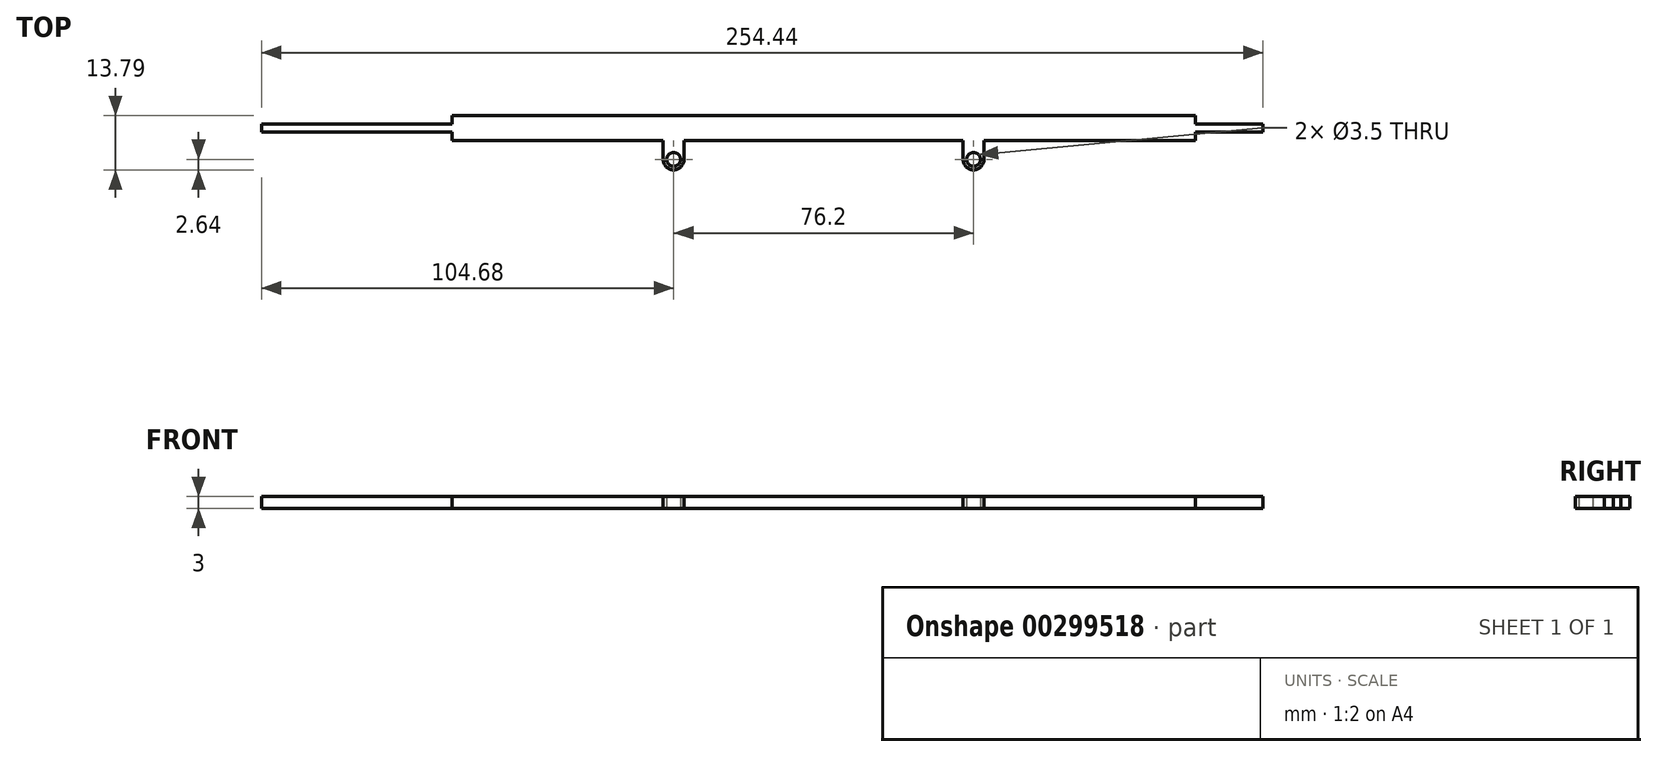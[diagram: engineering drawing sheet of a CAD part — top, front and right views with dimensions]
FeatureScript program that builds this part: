
annotation { "Feature Type Name" : "Feature", "Feature Type Description" : "" }
export const myFeature = defineFeature(function(context is Context, id is Id, definition is map)
    precondition{}
    {
        {
            var Q0;
            Q0=qCreatedBy(makeId("Top.planeOp"),FACE);
            var sketch = newSketch(context, id + "F0", { "sketchPlane" : qUnion([Q0])});
            skLineSegment(sketch, "E0.bottom", {"start": v(129.86, 3.2) * mm, "end": v(-129.86, 3.2) * mm});
            skLineSegment(sketch, "E0.top", {"start": v(129.86, -3.2) * mm, "end": v(-129.86, -3.2) * mm});
            skLineSegment(sketch, "E0.left", {"start": v(129.86, 3.2) * mm, "end": v(129.86, -3.2) * mm});
            skLineSegment(sketch, "E0.right", {"start": v(-129.86, 3.2) * mm, "end": v(-129.86, -3.2) * mm});
            skPoint(sketch, "E0.middle", {"position": v(0, 0) * mm});
            skSolve(sketch);
        }
        {
            var Q0;
            Q0=makeQuery(id+"F0.imprint","IMPRINT",FACE,{"disambiguationData":[TD([[makeQuery(id+"F0.imprint","IMPRINT",EDGE,{"derivedFrom":sQuery(id+"F0.wireOp",EDGE,"E0.bottom")}),1.0]])]});
            extrude(context, id + "F1", {"entities" : qUnion([Q0]), "depth" : 3 * mm});
        }
        {
            var Q0;
            Q0=qCreatedBy(makeId("Top.planeOp"),FACE);
            var sketch = newSketch(context, id + "F2", { "sketchPlane" : qUnion([Q0])});
            skLineSegment(sketch, "E1.bottom", {"start": v(129.86, -3.2) * mm, "end": v(124.58, -3.2) * mm});
            skLineSegment(sketch, "E1.top", {"start": v(129.86, -10.59) * mm, "end": v(124.58, -10.59) * mm});
            skLineSegment(sketch, "E1.left", {"start": v(129.86, -3.2) * mm, "end": v(129.86, -10.59) * mm});
            skLineSegment(sketch, "E1.right", {"start": v(124.58, -3.2) * mm, "end": v(124.58, -10.59) * mm});
            skCircle(sketch, "E2", {"center": v(127.22, -7.95) * mm, "radius": 1.75 * mm});
            skLineSegment(sketch, "E3", {"start": v(127.22, -7.95) * mm, "end": v(127.22, -10.59) * mm});
            skLineSegment(sketch, "E4", {"start": v(127.22, -7.95) * mm, "end": v(124.58, -7.95) * mm});
            skLineSegment(sketch, "E5.bottom", {"start": v(53.66, -3.2) * mm, "end": v(48.38, -3.2) * mm});
            skLineSegment(sketch, "E5.top", {"start": v(53.66, -10.59) * mm, "end": v(48.38, -10.59) * mm});
            skLineSegment(sketch, "E5.left", {"start": v(53.66, -3.2) * mm, "end": v(53.66, -10.59) * mm});
            skLineSegment(sketch, "E5.right", {"start": v(48.38, -3.2) * mm, "end": v(48.38, -10.6) * mm});
            skCircle(sketch, "E6", {"center": v(51.02, -7.95) * mm, "radius": 1.75 * mm});
            skPoint(sketch, "E6.centerSnap0", {"position": v(51.02, -10.6) * mm});
            skLineSegment(sketch, "E7", {"start": v(51.02, -7.95) * mm, "end": v(48.38, -7.95) * mm});
            skPoint(sketch, "E7.endSnap0", {"position": v(48.38, -6.9) * mm});
            skLineSegment(sketch, "E8.bottom", {"start": v(-27.82, -3.2) * mm, "end": v(-22.54, -3.2) * mm});
            skLineSegment(sketch, "E8.top", {"start": v(-27.82, -10.6) * mm, "end": v(-22.54, -10.6) * mm});
            skLineSegment(sketch, "E8.left", {"start": v(-27.82, -3.2) * mm, "end": v(-27.82, -10.6) * mm});
            skLineSegment(sketch, "E8.right", {"start": v(-22.54, -3.2) * mm, "end": v(-22.54, -10.6) * mm});
            skCircle(sketch, "E9", {"center": v(-25.18, -7.95) * mm, "radius": 1.75 * mm});
            skLineSegment(sketch, "E10", {"start": v(-25.18, -7.95) * mm, "end": v(-27.82, -7.95) * mm});
            skSolve(sketch);
        }
        {
            var Q0;
            {var subQ1=sQuery(id+"F2.wireOp",EDGE,"E1.bottom");Q0=makeQuery(id+"F2.imprint","IMPRINT",FACE,{"disambiguationData":[TD([[makeQuery(id+"F2.imprint","IMPRINT",EDGE,{"derivedFrom":subQ1}),1.0]])]});}
            var Q1;
            {var subQ1=sQuery(id+"F2.wireOp",EDGE,"E1.top");var subQ7=sQuery(id+"F2.wireOp",EDGE,"E1.right");var subQ8=makeQuery(id+"F2.imprint","INTERSECT",VERTEX,{"derivedFrom":[subQ1,subQ7]});Q1=makeQuery(id+"F2.imprint","IMPRINT",FACE,{"disambiguationData":[TD([[makeQuery(id+"F2.imprint","IMPRINT",EDGE,{"disambiguationData":[TD([[subQ8,1.0]])],"derivedFrom":subQ1}),-1.0]])]});}
            var Q2;
            {var subQ1=sQuery(id+"F2.wireOp",EDGE,"E5.bottom");Q2=makeQuery(id+"F2.imprint","IMPRINT",FACE,{"disambiguationData":[TD([[makeQuery(id+"F2.imprint","IMPRINT",EDGE,{"derivedFrom":subQ1}),1.0]])]});}
            var Q3;
            {var subQ3=sQuery(id+"F2.wireOp",EDGE,"E8.bottom");Q3=makeQuery(id+"F2.imprint","IMPRINT",FACE,{"disambiguationData":[TD([[makeQuery(id+"F2.imprint","IMPRINT",EDGE,{"derivedFrom":subQ3}),-1.0]])]});}
            extrude(context, id + "F3", {"entities" : qUnion([Q0, Q1, Q2, Q3]), "operationType" : NewBodyOperationType.ADD, "depth" : 3 * mm});
        }
        {
            var Q0;
            Q0=makeQuery(id+"F3.opExtrude","SWEPT_EDGE",EDGE,{"disambiguationData":[OSD([sQuery(id+"F2.wireOp",EDGE,"E5.top"),sQuery(id+"F2.wireOp",EDGE,"E5.right")])]});
            var Q1;
            Q1=makeQuery(id+"F3.opExtrude","SWEPT_EDGE",EDGE,{"disambiguationData":[OSD([sQuery(id+"F2.wireOp",EDGE,"E5.top"),sQuery(id+"F2.wireOp",EDGE,"E5.left")])]});
            var Q2;
            Q2=makeQuery(id+"F3.opExtrude","SWEPT_EDGE",EDGE,{"disambiguationData":[OSD([sQuery(id+"F2.wireOp",EDGE,"E1.top"),sQuery(id+"F2.wireOp",EDGE,"E1.right")])]});
            var Q3;
            Q3=makeQuery(id+"F3.opExtrude","SWEPT_EDGE",EDGE,{"disambiguationData":[OSD([sQuery(id+"F2.wireOp",EDGE,"E1.top"),sQuery(id+"F2.wireOp",EDGE,"E1.left")])]});
            var Q4;
            Q4=makeQuery(id+"F3.opExtrude","SWEPT_EDGE",EDGE,{"disambiguationData":[OSD([sQuery(id+"F2.wireOp",EDGE,"E8.top"),sQuery(id+"F2.wireOp",EDGE,"E8.left")])]});
            var Q5;
            Q5=makeQuery(id+"F3.opExtrude","SWEPT_EDGE",EDGE,{"disambiguationData":[OSD([sQuery(id+"F2.wireOp",EDGE,"E8.top"),sQuery(id+"F2.wireOp",EDGE,"E8.right")])]});
            fillet(context, id + "F4", {"entities" : qUnion([Q0, Q1, Q2, Q3, Q4, Q5]), "radius" : 2.64 * mm, "tangentPropagation" : true, "allowEdgeOverflow" : false});
        }
        {
            var Q0;
            Q0=makeQuery(id+"F3.boolean.opBoolean","MERGE",FACE,{"derivedFrom":[makeQuery(id+"F1.opExtrude","CAP_FACE",FACE,{"disambiguationData":[OSD([sQuery(id+"F0.wireOp",EDGE,"E0.bottom"),sQuery(id+"F0.wireOp",EDGE,"E0.top"),sQuery(id+"F0.wireOp",EDGE,"E0.left"),sQuery(id+"F0.wireOp",EDGE,"E0.right")])],"isStart":false}),makeQuery(id+"F3.opExtrude","CAP_FACE",FACE,{"disambiguationData":[OSD([sQuery(id+"F2.wireOp",EDGE,"E1.bottom"),sQuery(id+"F2.wireOp",EDGE,"E1.top"),sQuery(id+"F2.wireOp",EDGE,"E1.left"),sQuery(id+"F2.wireOp",EDGE,"E1.right"),sQuery(id+"F2.wireOp",EDGE,"E2")])],"isStart":false}),makeQuery(id+"F3.opExtrude","CAP_FACE",FACE,{"disambiguationData":[OSD([sQuery(id+"F2.wireOp",EDGE,"E5.bottom"),sQuery(id+"F2.wireOp",EDGE,"E5.top"),sQuery(id+"F2.wireOp",EDGE,"E5.left"),sQuery(id+"F2.wireOp",EDGE,"E5.right"),sQuery(id+"F2.wireOp",EDGE,"E6")])],"isStart":false}),makeQuery(id+"F3.opExtrude","CAP_FACE",FACE,{"disambiguationData":[OSD([sQuery(id+"F2.wireOp",EDGE,"E8.bottom"),sQuery(id+"F2.wireOp",EDGE,"E8.top"),sQuery(id+"F2.wireOp",EDGE,"E8.left"),sQuery(id+"F2.wireOp",EDGE,"E8.right"),sQuery(id+"F2.wireOp",EDGE,"E9")])],"isStart":false})]});
            var sketch = newSketch(context, id + "F5", { "sketchPlane" : qUnion([Q0])});
            skLineSegment(sketch, "E11.bottom", {"start": v(107.33, 1) * mm, "end": v(124.58, 1) * mm});
            skLineSegment(sketch, "E11.top", {"start": v(107.33, 3.2) * mm, "end": v(124.58, 3.2) * mm});
            skLineSegment(sketch, "E11.left", {"start": v(107.33, 1) * mm, "end": v(107.33, 3.2) * mm});
            skLineSegment(sketch, "E11.right", {"start": v(124.58, 1) * mm, "end": v(124.58, 3.2) * mm});
            skLineSegment(sketch, "E12.bottom", {"start": v(107.33, -3.2) * mm, "end": v(124.58, -3.2) * mm});
            skLineSegment(sketch, "E12.top", {"start": v(107.33, -1) * mm, "end": v(124.58, -1) * mm});
            skLineSegment(sketch, "E12.left", {"start": v(107.33, -3.2) * mm, "end": v(107.33, -1) * mm});
            skLineSegment(sketch, "E12.right", {"start": v(124.58, -3.2) * mm, "end": v(124.58, -1) * mm});
            skLineSegment(sketch, "E13.bottom", {"start": v(124.58, 3.2) * mm, "end": v(129.86, 3.2) * mm});
            skLineSegment(sketch, "E13.top", {"start": v(124.58, -10.59) * mm, "end": v(129.86, -10.59) * mm});
            skLineSegment(sketch, "E13.left", {"start": v(124.58, 3.2) * mm, "end": v(124.58, -10.59) * mm});
            skLineSegment(sketch, "E13.right", {"start": v(129.86, 3.2) * mm, "end": v(129.86, -10.59) * mm});
            skSolve(sketch);
        }
        {
            var Q0;
            {var subQ3=sQuery(id+"F5.wireOp",EDGE,"E13.bottom");Q0=makeQuery(id+"F5.imprint","IMPRINT",FACE,{"disambiguationData":[TD([[makeQuery(id+"F5.imprint","IMPRINT",EDGE,{"derivedFrom":subQ3}),1.0]])]});}
            var Q1;
            {var subQ0=sQuery(id+"F5.wireOp",EDGE,"E11.bottom");Q1=makeQuery(id+"F5.imprint","IMPRINT",FACE,{"disambiguationData":[TD([[makeQuery(id+"F5.imprint","IMPRINT",EDGE,{"derivedFrom":subQ0}),1.0]])]});}
            var Q2;
            {var subQ0=sQuery(id+"F5.wireOp",EDGE,"E12.bottom");Q2=makeQuery(id+"F5.imprint","IMPRINT",FACE,{"disambiguationData":[TD([[makeQuery(id+"F5.imprint","IMPRINT",EDGE,{"derivedFrom":subQ0}),-1.0]])]});}
            extrude(context, id + "F6", {"entities" : qUnion([Q0, Q1, Q2]), "operationType" : NewBodyOperationType.REMOVE, "endBound" : BoundingType.THROUGH_ALL, "oppositeDirection" : true, "depth" : 25 * mm});
        }
        {
            var Q0;
            Q0=makeQuery(id+"F3.boolean.opBoolean","MERGE",FACE,{"derivedFrom":[makeQuery(id+"F1.opExtrude","CAP_FACE",FACE,{"disambiguationData":[OSD([sQuery(id+"F0.wireOp",EDGE,"E0.bottom"),sQuery(id+"F0.wireOp",EDGE,"E0.top"),sQuery(id+"F0.wireOp",EDGE,"E0.left"),sQuery(id+"F0.wireOp",EDGE,"E0.right")])],"isStart":false}),makeQuery(id+"F3.opExtrude","CAP_FACE",FACE,{"disambiguationData":[OSD([sQuery(id+"F2.wireOp",EDGE,"E1.bottom"),sQuery(id+"F2.wireOp",EDGE,"E1.top"),sQuery(id+"F2.wireOp",EDGE,"E1.left"),sQuery(id+"F2.wireOp",EDGE,"E1.right"),sQuery(id+"F2.wireOp",EDGE,"E2")])],"isStart":false}),makeQuery(id+"F3.opExtrude","CAP_FACE",FACE,{"disambiguationData":[OSD([sQuery(id+"F2.wireOp",EDGE,"E5.bottom"),sQuery(id+"F2.wireOp",EDGE,"E5.top"),sQuery(id+"F2.wireOp",EDGE,"E5.left"),sQuery(id+"F2.wireOp",EDGE,"E5.right"),sQuery(id+"F2.wireOp",EDGE,"E6")])],"isStart":false}),makeQuery(id+"F3.opExtrude","CAP_FACE",FACE,{"disambiguationData":[OSD([sQuery(id+"F2.wireOp",EDGE,"E8.bottom"),sQuery(id+"F2.wireOp",EDGE,"E8.top"),sQuery(id+"F2.wireOp",EDGE,"E8.left"),sQuery(id+"F2.wireOp",EDGE,"E8.right"),sQuery(id+"F2.wireOp",EDGE,"E9")])],"isStart":false})]});
            var sketch = newSketch(context, id + "F7", { "sketchPlane" : qUnion([Q0])});
            skLineSegment(sketch, "E14.bottom", {"start": v(-129.86, -3.2) * mm, "end": v(-81.49, -3.2) * mm});
            skLineSegment(sketch, "E14.top", {"start": v(-129.86, -1) * mm, "end": v(-81.49, -1) * mm});
            skLineSegment(sketch, "E14.left", {"start": v(-129.86, -3.2) * mm, "end": v(-129.86, -1) * mm});
            skLineSegment(sketch, "E14.right", {"start": v(-81.49, -3.2) * mm, "end": v(-81.49, -1) * mm});
            skLineSegment(sketch, "E15.bottom", {"start": v(-129.86, 3.2) * mm, "end": v(-81.49, 3.2) * mm});
            skLineSegment(sketch, "E15.top", {"start": v(-129.86, 1) * mm, "end": v(-81.49, 1) * mm});
            skLineSegment(sketch, "E15.left", {"start": v(-129.86, 3.2) * mm, "end": v(-129.86, 1) * mm});
            skLineSegment(sketch, "E15.right", {"start": v(-81.49, 3.2) * mm, "end": v(-81.49, 1) * mm});
            skLineSegment(sketch, "E16", {"start": v(-81.49, -3.2) * mm, "end": v(-27.82, -3.2) * mm});
            skLineSegment(sketch, "E17.bottom", {"start": v(-129.86, -1) * mm, "end": v(-98.74, -1) * mm});
            skLineSegment(sketch, "E17.top", {"start": v(-129.86, 1) * mm, "end": v(-98.74, 1) * mm});
            skLineSegment(sketch, "E17.left", {"start": v(-129.86, -1) * mm, "end": v(-129.86, 1) * mm});
            skLineSegment(sketch, "E17.right", {"start": v(-98.74, -1) * mm, "end": v(-98.74, 1) * mm});
            skSolve(sketch);
        }
        {
            var Q0;
            Q0=makeQuery(id+"F7.imprint","IMPRINT",FACE,{"disambiguationData":[TD([[makeQuery(id+"F7.imprint","IMPRINT",EDGE,{"derivedFrom":sQuery(id+"F7.wireOp",EDGE,"E15.bottom")}),1.0]])]});
            var Q1;
            Q1=makeQuery(id+"F7.imprint","IMPRINT",FACE,{"disambiguationData":[TD([[makeQuery(id+"F7.imprint","IMPRINT",EDGE,{"derivedFrom":sQuery(id+"F7.wireOp",EDGE,"E14.bottom")}),-1.0]])]});
            var Q2;
            Q2=makeQuery(id+"F7.imprint","IMPRINT",FACE,{"disambiguationData":[TD([[makeQuery(id+"F7.imprint","IMPRINT",EDGE,{"derivedFrom":sQuery(id+"F7.wireOp",EDGE,"E17.bottom")}),1.0]])]});
            extrude(context, id + "F8", {"entities" : qUnion([Q0, Q1, Q2]), "operationType" : NewBodyOperationType.REMOVE, "endBound" : BoundingType.THROUGH_ALL, "oppositeDirection" : true, "depth" : 25 * mm});
        }
    });
